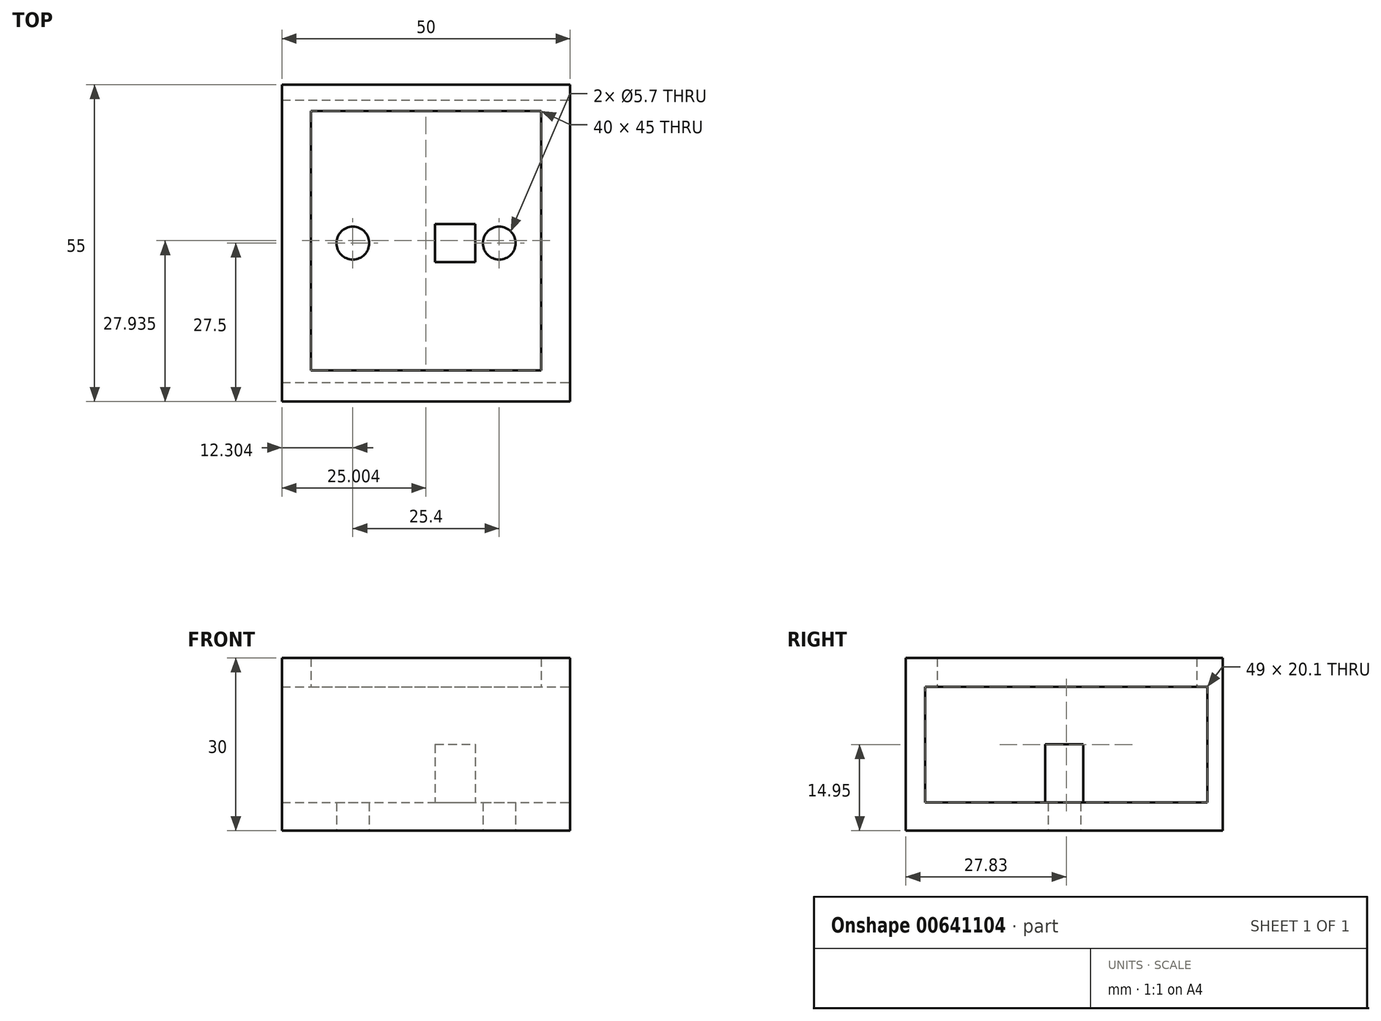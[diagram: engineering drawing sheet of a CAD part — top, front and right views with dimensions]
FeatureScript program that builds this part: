
annotation { "Feature Type Name" : "Feature", "Feature Type Description" : "" }
export const myFeature = defineFeature(function(context is Context, id is Id, definition is map)
    precondition{}
    {
        {
            var Q0;
            Q0=qCreatedBy(makeId("Top.planeOp"),FACE);
            var sketch = newSketch(context, id + "F0", { "sketchPlane" : qUnion([Q0])});
            skLineSegment(sketch, "E0.bottom", {"start": v(-68.75, -6.1) * mm, "end": v(-28.75, -6.1) * mm});
            skLineSegment(sketch, "E0.top", {"start": v(-68.75, -50.22) * mm, "end": v(-28.75, -50.22) * mm});
            skLineSegment(sketch, "E0.left", {"start": v(-68.75, -6.1) * mm, "end": v(-68.75, -50.22) * mm});
            skLineSegment(sketch, "E0.right", {"start": v(-28.75, -6.1) * mm, "end": v(-28.75, -50.22) * mm});
            skCircle(sketch, "E1", {"center": v(-61.45, -28.16) * mm, "radius": 2.85 * mm});
            skCircle(sketch, "E2", {"center": v(-36.05, -28.16) * mm, "radius": 2.85 * mm});
            skLineSegment(sketch, "E3.bottom", {"start": v(-47.18, -24.86) * mm, "end": v(-40.18, -24.86) * mm});
            skLineSegment(sketch, "E3.top", {"start": v(-47.18, -31.46) * mm, "end": v(-40.18, -31.46) * mm});
            skLineSegment(sketch, "E3.left", {"start": v(-47.18, -24.86) * mm, "end": v(-47.18, -31.46) * mm});
            skLineSegment(sketch, "E3.right", {"start": v(-40.18, -24.86) * mm, "end": v(-40.18, -31.46) * mm});
            skSolve(sketch);
        }
        {
            var Q0;
            Q0=qCreatedBy(makeId("Top.planeOp"),FACE);
            var sketch = newSketch(context, id + "F1", { "sketchPlane" : qUnion([Q0])});
            skLineSegment(sketch, "E4.bottom", {"start": v(-68.75, -50.22) * mm, "end": v(-28.75, -50.22) * mm});
            skLineSegment(sketch, "E4.top", {"start": v(-68.75, -5.22) * mm, "end": v(-28.75, -5.22) * mm});
            skLineSegment(sketch, "E4.left", {"start": v(-68.75, -50.22) * mm, "end": v(-68.75, -5.22) * mm});
            skLineSegment(sketch, "E4.right", {"start": v(-28.75, -50.22) * mm, "end": v(-28.75, -5.22) * mm});
            skSolve(sketch);
        }
        {
            var Q0;
            Q0=qCreatedBy(makeId("Top.planeOp"),FACE);
            var sketch = newSketch(context, id + "F2", { "sketchPlane" : qUnion([Q0])});
            skLineSegment(sketch, "E5.bottom", {"start": v(-73.75, -0.66) * mm, "end": v(-23.75, -0.66) * mm});
            skLineSegment(sketch, "E5.top", {"start": v(-73.75, -55.66) * mm, "end": v(-23.75, -55.66) * mm});
            skLineSegment(sketch, "E5.left", {"start": v(-73.75, -0.66) * mm, "end": v(-73.75, -55.66) * mm});
            skLineSegment(sketch, "E5.right", {"start": v(-23.75, -0.66) * mm, "end": v(-23.75, -55.66) * mm});
            skSolve(sketch);
        }
        {
            var Q0;
            Q0=makeQuery(id+"F2.imprint","IMPRINT",FACE,{"disambiguationData":[TD([[makeQuery(id+"F2.imprint","IMPRINT",EDGE,{"derivedFrom":sQuery(id+"F2.wireOp",EDGE,"E5.bottom")}),-1.0]])]});
            extrude(context, id + "F3", {"entities" : qUnion([Q0]), "depth" : 30 * mm, "offsetDistance" : 25 * mm});
        }
        {
            var Q0;
            Q0=makeQuery(id+"F3.opExtrude","SWEPT_FACE",FACE,{"disambiguationData":[OSD([sQuery(id+"F2.wireOp",EDGE,"E5.right")])]});
            var sketch = newSketch(context, id + "F4", { "sketchPlane" : qUnion([Q0])});
            skLineSegment(sketch, "E6.bottom", {"start": v(-52.33, 25) * mm, "end": v(-3.33, 25) * mm});
            skLineSegment(sketch, "E6.top", {"start": v(-52.33, 4.9) * mm, "end": v(-3.33, 4.9) * mm});
            skLineSegment(sketch, "E6.left", {"start": v(-52.33, 25) * mm, "end": v(-52.33, 4.9) * mm});
            skLineSegment(sketch, "E6.right", {"start": v(-3.33, 25) * mm, "end": v(-3.33, 4.9) * mm});
            skSolve(sketch);
        }
        {
            var Q0;
            Q0=makeQuery(id+"F4.imprint","IMPRINT",FACE,{"disambiguationData":[TD([[makeQuery(id+"F4.imprint","IMPRINT",EDGE,{"derivedFrom":sQuery(id+"F4.wireOp",EDGE,"E6.bottom")}),-1.0]])]});
            extrude(context, id + "F5", {"entities" : qUnion([Q0]), "operationType" : NewBodyOperationType.REMOVE, "endBound" : BoundingType.THROUGH_ALL, "oppositeDirection" : true, "depth" : 25 * mm, "offsetDistance" : 25 * mm});
        }
        {
            var Q0;
            Q0=makeQuery(id+"F0.imprint","IMPRINT",FACE,{"disambiguationData":[TD([[makeQuery(id+"F0.imprint","IMPRINT",EDGE,{"derivedFrom":sQuery(id+"F0.wireOp",EDGE,"E2")}),1.0]])]});
            var Q1;
            Q1=makeQuery(id+"F0.imprint","IMPRINT",FACE,{"disambiguationData":[TD([[makeQuery(id+"F0.imprint","IMPRINT",EDGE,{"derivedFrom":sQuery(id+"F0.wireOp",EDGE,"6642a22c-2b82-4595-b8f3-f01fc690ecbd")}),1.0]])]});
            var Q2;
            Q2=makeQuery(id+"F0.imprint","IMPRINT",FACE,{"disambiguationData":[TD([[makeQuery(id+"F0.imprint","IMPRINT",EDGE,{"derivedFrom":sQuery(id+"F0.wireOp",EDGE,"E1")}),1.0]])]});
            var Q3;
            Q3=makeQuery(id+"F0.imprint","IMPRINT",FACE,{"disambiguationData":[TD([[makeQuery(id+"F0.imprint","IMPRINT",EDGE,{"derivedFrom":sQuery(id+"F0.wireOp",EDGE,"7c57296f-aef0-4abf-913d-f533830c059c")}),1.0]])]});
            extrude(context, id + "F6", {"entities" : qUnion([Q0, Q1, Q2, Q3]), "operationType" : NewBodyOperationType.REMOVE, "endBound" : BoundingType.UP_TO_NEXT, "depth" : 25 * mm, "offsetDistance" : 25 * mm});
        }
        {
            var Q0;
            Q0=makeQuery(id+"F0.imprint","IMPRINT",FACE,{"disambiguationData":[TD([[makeQuery(id+"F0.imprint","IMPRINT",EDGE,{"derivedFrom":sQuery(id+"F0.wireOp",EDGE,"E3.bottom")}),-1.0]])]});
            extrude(context, id + "F7", {"entities" : qUnion([Q0]), "operationType" : NewBodyOperationType.ADD, "depth" : 15 * mm, "offsetDistance" : 25 * mm});
        }
        {
            var Q0;
            Q0=makeQuery(id+"F1.imprint","IMPRINT",FACE,{"disambiguationData":[TD([[makeQuery(id+"F1.imprint","IMPRINT",EDGE,{"derivedFrom":sQuery(id+"F1.wireOp",EDGE,"E4.bottom")}),1.0]])]});
            extrude(context, id + "F8", {"entities" : qUnion([Q0]), "operationType" : NewBodyOperationType.REMOVE, "depth" : 50 * mm, "hasOffset" : true, "offsetDistance" : 20 * mm, "hasSecondDirection" : true, "secondDirectionOppositeDirection" : false, "secondDirectionDepth" : 25 * mm});
        }
    });
